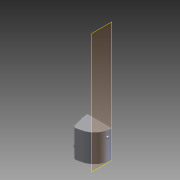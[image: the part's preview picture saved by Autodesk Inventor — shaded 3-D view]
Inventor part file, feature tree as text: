
AUTODESK INVENTOR PART (.ipt)
format: ipt  version: 2012 SP2 (Build 160219200, 219)  size: 151,040 bytes
history: native  units: in
note: dims shown in document units (in); Inventor stores cm internally (conversion verified against a paired STEP export)
features: extrude x6, sketch x6, fillet x2, chamfer x1, plane x1
ambient origin geometry x8: Origin, YZ Plane, XZ Plane, XY Plane, X Axis, Y Axis, Z Axis, Center Point
bodies: Solid1 (feature_tree)
feature tree (16):
  extrude  "Extrusion1"  Depth=11.9375in TaperAngle=0.0deg
  extrude  "Extrusion2"  Depth=0.5in TaperAngle=0.0deg
  extrude  "Extrusion3"  Depth=3.4466in
  extrude  "Extrusion4"  Depth=0.5in TaperAngle=0.0deg
  extrude  "Extrusion5"  Depth=0.1875in
  fillet  "Fillet1"  Radius=4.6875in
  fillet  "Fillet2"  Radius=0.5in
  chamfer  "Chamfer1"  [1 undecoded]
  plane  "Work Plane1"
  extrude  "Extrusion6"  [1 undecoded]
  sketch  "Sketch1"  dims[d0=5.6875in d1=0.0in d2=11.9375in d3=0.0in]
  sketch  "Sketch2"  dims[d4=1.1811in d6=1.2in d7=0.3937in d9=1.0in d11=0.5in d12=0.0in]
  sketch  "Sketch3"  dims[d13=0.5in d14=0.0in d15=3.4466in]
  sketch  "Sketch4"  dims[d16=2.2892in d17=0.5in d18=0.0in]
  sketch  "Sketch5"  dims[d19=5.125in d20=0.1875in]
  sketch  "Sketch6"  dims[d21=0.5625in d22=0.125in d23=45.0deg d24=4.6875in d25=0.5in d26=0.0in]
note: 2 required parameter values undecoded (feature->parameter linkage not recoverable at this tier; creation-order binding heuristic only, values carry confidence <= 0.55)
